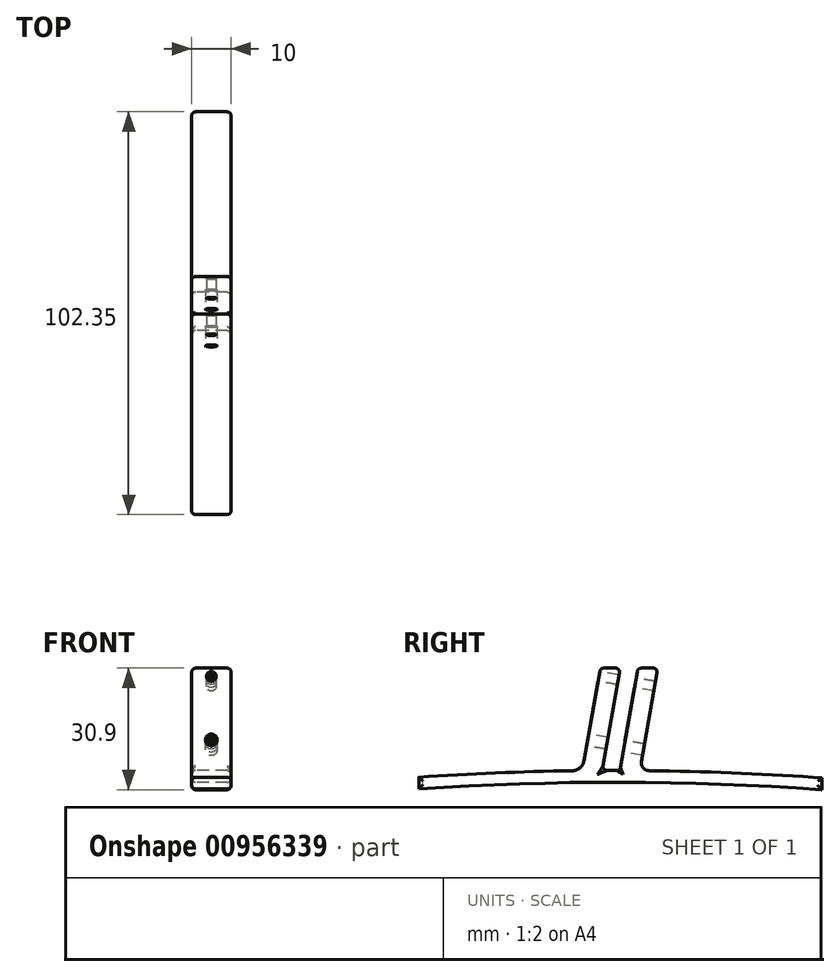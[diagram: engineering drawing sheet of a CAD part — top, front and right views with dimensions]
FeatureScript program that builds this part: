
annotation { "Feature Type Name" : "Feature", "Feature Type Description" : "" }
export const myFeature = defineFeature(function(context is Context, id is Id, definition is map)
    precondition{}
    {
        {
            var Q0;
            Q0=qCreatedBy(makeId("Right.planeOp"),FACE);
            var sketch = newSketch(context, id + "F0", { "sketchPlane" : qUnion([Q0])});
            skLineSegment(sketch, "E0.top", {"start": v(1.49, 30.73) * mm, "end": v(6.57, 30.73) * mm});
            skLineSegment(sketch, "E0.left", {"start": v(-44.6, 0) * mm, "end": v(-44.6, 3) * mm});
            skLineSegment(sketch, "E0.right", {"start": v(57.74, -0.17) * mm, "end": v(57.74, 2.84) * mm});
            skLineSegment(sketch, "E1", {"start": v(6.57, 30.73) * mm, "end": v(1.98, 4.72) * mm});
            skLineSegment(sketch, "E2", {"start": v(1.2, 0.27) * mm, "end": v(1.2, 36.45) * mm, "construction": true});
            skArc(sketch, "E3", {"start": v(57.74, -0.17) * mm, "mid": v(6.57, 1.73) * mm, "end": v(-44.6, 0) * mm});
            skLineSegment(sketch, "E4", {"start": v(11.03, 30.73) * mm, "end": v(6.45, 4.73) * mm});
            skLineSegment(sketch, "E5", {"start": v(1.49, 30.73) * mm, "end": v(-3.1, 4.68) * mm});
            skLineSegment(sketch, "E6", {"start": v(16.11, 30.73) * mm, "end": v(11.52, 4.7) * mm});
            skArc(sketch, "E7.0", {"start": v(55.6, 3) * mm, "mid": v(33.57, 4.18) * mm, "end": v(11.52, 4.7) * mm});
            skPoint(sketch, "E8.orphan", {"position": v(-44.6, 30.73) * mm});
            skLineSegment(sketch, "E9.trimOffspring", {"start": v(11.03, 30.73) * mm, "end": v(16.11, 30.73) * mm});
            skPoint(sketch, "E10.orphan", {"position": v(57.74, 30.73) * mm});
            skArc(sketch, "E11.trimOffspring", {"start": v(6.45, 4.73) * mm, "mid": v(3.82, 4.73) * mm, "end": v(1.2, 4.72) * mm});
            skArc(sketch, "E12.trimOffspring", {"start": v(-3.1, 4.68) * mm, "mid": v(-23.97, 4.14) * mm, "end": v(-44.81, 3) * mm});
            skPoint(sketch, "E13.orphan", {"position": v(-3.18, 4.24) * mm});
            skPoint(sketch, "E14.orphan", {"position": v(11.44, 4.24) * mm});
            skLineSegment(sketch, "E15", {"start": v(55.6, 3) * mm, "end": v(57.74, 2.84) * mm});
            skSolve(sketch);
        }
        {
            var Q0;
            {var subQ6=sQuery(id+"F0.wireOp",EDGE,"E0.top");Q0=makeQuery(id+"F0.imprint","IMPRINT",FACE,{"disambiguationData":[TD([[makeQuery(id+"F0.imprint","IMPRINT",EDGE,{"derivedFrom":subQ6}),-1.0]])]});}
            extrude(context, id + "F1", {"entities" : qUnion([Q0]), "endBound" : BoundingType.SYMMETRIC, "depth" : 10 * mm, "offsetDistance" : 25 * mm});
        }
        {
            var Q0;
            Q0=makeQuery(id+"F1.opExtrude","SWEPT_FACE",FACE,{"disambiguationData":[OSD([sQuery(id+"F0.wireOp",EDGE,"E5")])]});
            var sketch = newSketch(context, id + "F2", { "sketchPlane" : qUnion([Q0])});
            skCircle(sketch, "E16", {"center": v(0, 12) * mm, "radius": 1.5 * mm});
            skCircle(sketch, "E17", {"center": v(0, 28.4) * mm, "radius": 1.25 * mm});
            skSolve(sketch);
        }
        {
            var Q0;
            Q0 = qSketchRegion(id + "F2", true);
            extrude(context, id + "F3", {"entities" : qUnion([Q0]), "operationType" : NewBodyOperationType.REMOVE, "oppositeDirection" : true, "depth" : 15 * mm, "offsetDistance" : 25 * mm});
        }
        {
            var Q0;
            Q0=makeQuery(id+"F1.opExtrude","SWEPT_EDGE",EDGE,{"disambiguationData":[OSD([sQuery(id+"F0.wireOp",EDGE,"E5"),sQuery(id+"F0.wireOp",EDGE,"E12.trimOffspring")])]});
            fillet(context, id + "F4", {"entities" : qUnion([Q0]), "radius" : 3 * mm, "tangentPropagation" : true, "allowEdgeOverflow" : false});
        }
        {
            var Q0;
            Q0=makeQuery(id+"F1.opExtrude","SWEPT_EDGE",EDGE,{"disambiguationData":[OSD([sQuery(id+"F0.wireOp",EDGE,"E6"),sQuery(id+"F0.wireOp",EDGE,"E7.0")])]});
            fillet(context, id + "F5", {"entities" : qUnion([Q0]), "radius" : 2 * mm, "tangentPropagation" : true, "allowEdgeOverflow" : false});
        }
        {
            var Q0;
            Q0=makeQuery(id+"F1.opExtrude","CAP_FACE",FACE,{"disambiguationData":[OSD([sQuery(id+"F0.wireOp",EDGE,"E0.top"),sQuery(id+"F0.wireOp",EDGE,"E0.left"),sQuery(id+"F0.wireOp",EDGE,"E0.right"),sQuery(id+"F0.wireOp",EDGE,"E1"),sQuery(id+"F0.wireOp",EDGE,"E3"),sQuery(id+"F0.wireOp",EDGE,"E4"),sQuery(id+"F0.wireOp",EDGE,"E5"),sQuery(id+"F0.wireOp",EDGE,"E6"),sQuery(id+"F0.wireOp",EDGE,"E7.0"),sQuery(id+"F0.wireOp",EDGE,"E9.trimOffspring"),sQuery(id+"F0.wireOp",EDGE,"E11.trimOffspring"),sQuery(id+"F0.wireOp",EDGE,"E12.trimOffspring"),sQuery(id+"F0.wireOp",EDGE,"E15")])],"isStart":false});
            var Q1;
            Q1=makeQuery(id+"F1.opExtrude","CAP_FACE",FACE,{"disambiguationData":[OSD([sQuery(id+"F0.wireOp",EDGE,"E0.top"),sQuery(id+"F0.wireOp",EDGE,"E0.left"),sQuery(id+"F0.wireOp",EDGE,"E0.right"),sQuery(id+"F0.wireOp",EDGE,"E1"),sQuery(id+"F0.wireOp",EDGE,"E3"),sQuery(id+"F0.wireOp",EDGE,"E4"),sQuery(id+"F0.wireOp",EDGE,"E5"),sQuery(id+"F0.wireOp",EDGE,"E6"),sQuery(id+"F0.wireOp",EDGE,"E7.0"),sQuery(id+"F0.wireOp",EDGE,"E9.trimOffspring"),sQuery(id+"F0.wireOp",EDGE,"E11.trimOffspring"),sQuery(id+"F0.wireOp",EDGE,"E12.trimOffspring"),sQuery(id+"F0.wireOp",EDGE,"E15")])],"isStart":true});
            var Q2;
            Q2=makeQuery(id+"F1.opExtrude","SWEPT_FACE",FACE,{"disambiguationData":[OSD([sQuery(id+"F0.wireOp",EDGE,"E0.top")])]});
            var Q3;
            Q3=makeQuery(id+"F1.opExtrude","SWEPT_FACE",FACE,{"disambiguationData":[OSD([sQuery(id+"F0.wireOp",EDGE,"E9.trimOffspring")])]});
            fillet(context, id + "F6", {"entities" : qUnion([Q0, Q1, Q2, Q3]), "radius" : 1 * mm, "tangentPropagation" : true, "allowEdgeOverflow" : false});
        }
        {
            var Q0;
            Q0=makeQuery(id+"F1.opExtrude","SWEPT_EDGE",EDGE,{"disambiguationData":[OSD([sQuery(id+"F0.wireOp",EDGE,"E4"),sQuery(id+"F0.wireOp",EDGE,"E11.trimOffspring")])]});
            var Q1;
            Q1=makeQuery(id+"F1.opExtrude","SWEPT_EDGE",EDGE,{"disambiguationData":[OSD([sQuery(id+"F0.wireOp",EDGE,"E1"),sQuery(id+"F0.wireOp",EDGE,"E11.trimOffspring")])]});
            fillet(context, id + "F7", {"entities" : qUnion([Q0, Q1]), "radius" : 1 * mm, "tangentPropagation" : true, "allowEdgeOverflow" : false});
        }
    });
